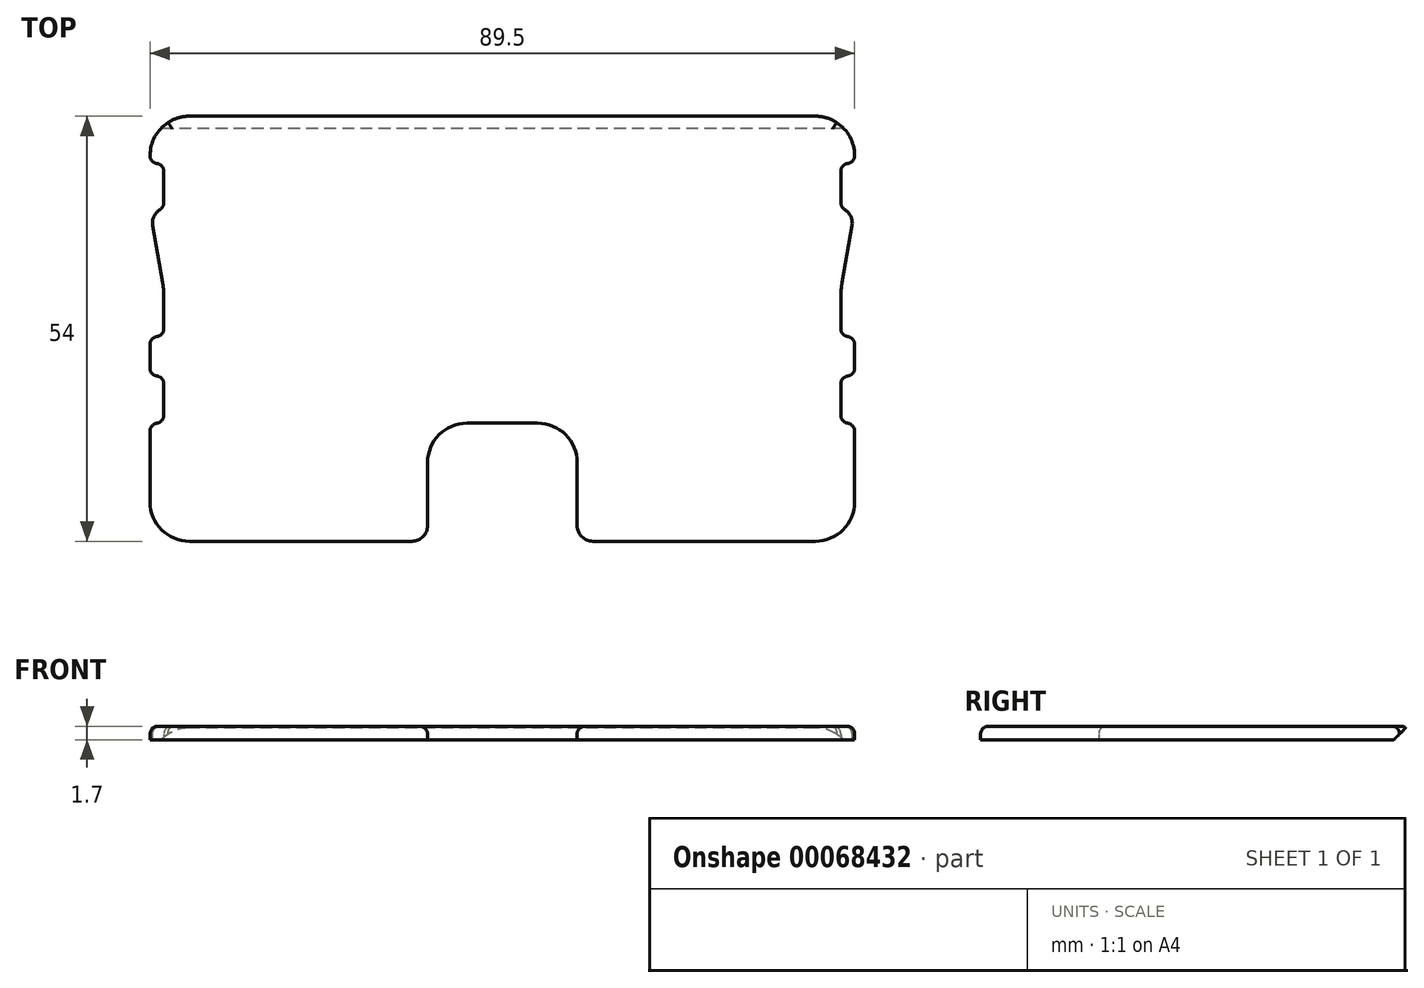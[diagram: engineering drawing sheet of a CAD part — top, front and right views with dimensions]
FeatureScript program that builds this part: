
annotation { "Feature Type Name" : "Feature", "Feature Type Description" : "" }
export const myFeature = defineFeature(function(context is Context, id is Id, definition is map)
    precondition{}
    {
        {
            var Q0;
            Q0=qCreatedBy(makeId("Top.planeOp"),FACE);
            var sketch = newSketch(context, id + "F0", { "sketchPlane" : qUnion([Q0])});
            skLineSegment(sketch, "E0", {"start": v(-44.75, -22.6) * mm, "end": v(-9.5, -22.6) * mm});
            skLineSegment(sketch, "E1", {"start": v(-9.5, -7.6) * mm, "end": v(9.5, -7.6) * mm});
            skLineSegment(sketch, "E2", {"start": v(9.5, -7.6) * mm, "end": v(9.5, -22.6) * mm});
            skLineSegment(sketch, "E3", {"start": v(9.5, -22.6) * mm, "end": v(44.75, -22.6) * mm});
            skLineSegment(sketch, "E4", {"start": v(44.75, -22.6) * mm, "end": v(44.75, -7.6) * mm});
            skLineSegment(sketch, "E5", {"start": v(44.75, -7.6) * mm, "end": v(43, -7.6) * mm});
            skLineSegment(sketch, "E6", {"start": v(43, -7.6) * mm, "end": v(43, -1.6) * mm});
            skLineSegment(sketch, "E7", {"start": v(43, -1.6) * mm, "end": v(44.75, -1.6) * mm});
            skLineSegment(sketch, "E8", {"start": v(44.75, -1.6) * mm, "end": v(44.75, 3.4) * mm});
            skLineSegment(sketch, "E9", {"start": v(44.75, 3.4) * mm, "end": v(43, 3.4) * mm});
            skLineSegment(sketch, "E10", {"start": v(43, 3.4) * mm, "end": v(43, 9.4) * mm});
            skLineSegment(sketch, "E11", {"start": v(43, 9.4) * mm, "end": v(44.75, 19.4) * mm});
            skPoint(sketch, "E11.endSnap0", {"position": v(44.75, 0.9) * mm});
            skLineSegment(sketch, "E12", {"start": v(44.75, 19.4) * mm, "end": v(43, 19.4) * mm});
            skPoint(sketch, "E12.endSnap0", {"position": v(43, 6.4) * mm});
            skLineSegment(sketch, "E13", {"start": v(43, 19.4) * mm, "end": v(43, 25.4) * mm});
            skLineSegment(sketch, "E14", {"start": v(43, 25.4) * mm, "end": v(44.75, 25.4) * mm});
            skLineSegment(sketch, "E15", {"start": v(44.75, 25.4) * mm, "end": v(44.75, 31.4) * mm});
            skLineSegment(sketch, "E16", {"start": v(44.75, 31.4) * mm, "end": v(-44.75, 31.4) * mm});
            skLineSegment(sketch, "E17", {"start": v(-44.75, 31.4) * mm, "end": v(-44.75, 25.4) * mm});
            skLineSegment(sketch, "E18", {"start": v(-44.75, 25.4) * mm, "end": v(-43, 25.4) * mm});
            skLineSegment(sketch, "E19", {"start": v(-43, 25.4) * mm, "end": v(-43, 19.4) * mm});
            skLineSegment(sketch, "E20", {"start": v(-43, 19.4) * mm, "end": v(-44.75, 19.4) * mm});
            skLineSegment(sketch, "E21", {"start": v(-44.75, 19.4) * mm, "end": v(-43, 9.4) * mm});
            skLineSegment(sketch, "E22", {"start": v(-43, 9.4) * mm, "end": v(-43, 3.4) * mm});
            skLineSegment(sketch, "E23", {"start": v(-43, 3.4) * mm, "end": v(-44.75, 3.4) * mm});
            skLineSegment(sketch, "E24", {"start": v(-44.75, 3.4) * mm, "end": v(-44.75, -1.6) * mm});
            skLineSegment(sketch, "E25", {"start": v(-44.75, -1.6) * mm, "end": v(-43, -1.6) * mm});
            skLineSegment(sketch, "E26", {"start": v(-43, -1.6) * mm, "end": v(-43, -7.6) * mm});
            skLineSegment(sketch, "E27", {"start": v(-43, -7.6) * mm, "end": v(-44.75, -7.6) * mm});
            skLineSegment(sketch, "E28", {"start": v(-44.75, -7.6) * mm, "end": v(-44.75, -22.6) * mm});
            skLineSegment(sketch, "E29", {"start": v(-9.5, -7.6) * mm, "end": v(-9.5, -22.6) * mm});
            skSolve(sketch);
        }
        {
            var Q0;
            Q0=makeQuery(id+"F0.imprint","IMPRINT",FACE,{"disambiguationData":[TD([[makeQuery(id+"F0.imprint","IMPRINT",EDGE,{"derivedFrom":sQuery(id+"F0.wireOp",EDGE,"E0")}),1.0]])]});
            extrude(context, id + "F1", {"entities" : qUnion([Q0]), "depth" : 1.7 * mm});
        }
        {
            var Q0;
            Q0=makeQuery(id+"F1.opExtrude","SWEPT_EDGE",EDGE,{"disambiguationData":[OSD([sQuery(id+"F0.wireOp",EDGE,"E18"),sQuery(id+"F0.wireOp",EDGE,"E19")])]});
            var Q1;
            Q1=makeQuery(id+"F1.opExtrude","SWEPT_EDGE",EDGE,{"disambiguationData":[OSD([sQuery(id+"F0.wireOp",EDGE,"E19"),sQuery(id+"F0.wireOp",EDGE,"E20")])]});
            var Q2;
            Q2=makeQuery(id+"F1.opExtrude","SWEPT_EDGE",EDGE,{"disambiguationData":[OSD([sQuery(id+"F0.wireOp",EDGE,"E22"),sQuery(id+"F0.wireOp",EDGE,"E23")])]});
            var Q3;
            Q3=makeQuery(id+"F1.opExtrude","SWEPT_EDGE",EDGE,{"disambiguationData":[OSD([sQuery(id+"F0.wireOp",EDGE,"E25"),sQuery(id+"F0.wireOp",EDGE,"E26")])]});
            var Q4;
            Q4=makeQuery(id+"F1.opExtrude","SWEPT_EDGE",EDGE,{"disambiguationData":[OSD([sQuery(id+"F0.wireOp",EDGE,"E26"),sQuery(id+"F0.wireOp",EDGE,"E27")])]});
            var Q5;
            Q5=makeQuery(id+"F1.opExtrude","SWEPT_EDGE",EDGE,{"disambiguationData":[OSD([sQuery(id+"F0.wireOp",EDGE,"E12"),sQuery(id+"F0.wireOp",EDGE,"E13")])]});
            var Q6;
            Q6=makeQuery(id+"F1.opExtrude","SWEPT_EDGE",EDGE,{"disambiguationData":[OSD([sQuery(id+"F0.wireOp",EDGE,"E13"),sQuery(id+"F0.wireOp",EDGE,"E14")])]});
            var Q7;
            Q7=makeQuery(id+"F1.opExtrude","SWEPT_EDGE",EDGE,{"disambiguationData":[OSD([sQuery(id+"F0.wireOp",EDGE,"E9"),sQuery(id+"F0.wireOp",EDGE,"E10")])]});
            var Q8;
            Q8=makeQuery(id+"F1.opExtrude","SWEPT_EDGE",EDGE,{"disambiguationData":[OSD([sQuery(id+"F0.wireOp",EDGE,"E5"),sQuery(id+"F0.wireOp",EDGE,"E6")])]});
            var Q9;
            Q9=makeQuery(id+"F1.opExtrude","SWEPT_EDGE",EDGE,{"disambiguationData":[OSD([sQuery(id+"F0.wireOp",EDGE,"E6"),sQuery(id+"F0.wireOp",EDGE,"E7")])]});
            fillet(context, id + "F2", {"entities" : qUnion([Q0, Q1, Q2, Q3, Q4, Q5, Q6, Q7, Q8, Q9]), "radius" : 1 * mm, "tangentPropagation" : true, "allowEdgeOverflow" : false});
        }
        {
            var Q0;
            Q0=makeQuery(id+"F1.opExtrude","SWEPT_EDGE",EDGE,{"disambiguationData":[OSD([sQuery(id+"F0.wireOp",EDGE,"E8"),sQuery(id+"F0.wireOp",EDGE,"E9")])]});
            var Q1;
            Q1=makeQuery(id+"F1.opExtrude","SWEPT_EDGE",EDGE,{"disambiguationData":[OSD([sQuery(id+"F0.wireOp",EDGE,"E4"),sQuery(id+"F0.wireOp",EDGE,"E5")])]});
            var Q2;
            Q2=makeQuery(id+"F1.opExtrude","SWEPT_EDGE",EDGE,{"disambiguationData":[OSD([sQuery(id+"F0.wireOp",EDGE,"E14"),sQuery(id+"F0.wireOp",EDGE,"E15")])]});
            var Q3;
            Q3=makeQuery(id+"F1.opExtrude","SWEPT_EDGE",EDGE,{"disambiguationData":[OSD([sQuery(id+"F0.wireOp",EDGE,"E7"),sQuery(id+"F0.wireOp",EDGE,"E8")])]});
            var Q4;
            Q4=makeQuery(id+"F1.opExtrude","SWEPT_EDGE",EDGE,{"disambiguationData":[OSD([sQuery(id+"F0.wireOp",EDGE,"E17"),sQuery(id+"F0.wireOp",EDGE,"E18")])]});
            var Q5;
            Q5=makeQuery(id+"F1.opExtrude","CAP_EDGE",EDGE,{"disambiguationData":[OSD([sQuery(id+"F0.wireOp",EDGE,"E26")])],"isStart":false});
            var Q6;
            Q6=makeQuery(id+"F1.opExtrude","CAP_EDGE",EDGE,{"disambiguationData":[OSD([sQuery(id+"F0.wireOp",EDGE,"E19")])],"isStart":false});
            var Q7;
            Q7=makeQuery(id+"F1.opExtrude","SWEPT_EDGE",EDGE,{"disambiguationData":[OSD([sQuery(id+"F0.wireOp",EDGE,"E24"),sQuery(id+"F0.wireOp",EDGE,"E25")])]});
            var Q8;
            Q8=makeQuery(id+"F1.opExtrude","SWEPT_EDGE",EDGE,{"disambiguationData":[OSD([sQuery(id+"F0.wireOp",EDGE,"E27"),sQuery(id+"F0.wireOp",EDGE,"E28")])]});
            var Q9;
            Q9=makeQuery(id+"F1.opExtrude","CAP_EDGE",EDGE,{"disambiguationData":[OSD([sQuery(id+"F0.wireOp",EDGE,"E13")])],"isStart":false});
            var Q10;
            Q10=makeQuery(id+"F1.opExtrude","CAP_EDGE",EDGE,{"disambiguationData":[OSD([sQuery(id+"F0.wireOp",EDGE,"E6")])],"isStart":false});
            var Q11;
            Q11=makeQuery(id+"F1.opExtrude","SWEPT_EDGE",EDGE,{"disambiguationData":[OSD([sQuery(id+"F0.wireOp",EDGE,"E23"),sQuery(id+"F0.wireOp",EDGE,"E24")])]});
            fillet(context, id + "F3", {"entities" : qUnion([Q0, Q1, Q2, Q3, Q4, Q5, Q6, Q7, Q8, Q9, Q10, Q11]), "radius" : 1 * mm, "tangentPropagation" : true, "allowEdgeOverflow" : false});
        }
        {
            var Q0;
            Q0=makeQuery(id+"F1.opExtrude","SWEPT_EDGE",EDGE,{"disambiguationData":[OSD([sQuery(id+"F0.wireOp",EDGE,"E21"),sQuery(id+"F0.wireOp",EDGE,"E22")])]});
            var Q1;
            Q1=makeQuery(id+"F1.opExtrude","SWEPT_EDGE",EDGE,{"disambiguationData":[OSD([sQuery(id+"F0.wireOp",EDGE,"E10"),sQuery(id+"F0.wireOp",EDGE,"E11")])]});
            fillet(context, id + "F4", {"entities" : qUnion([Q0, Q1]), "radius" : 10 * mm, "tangentPropagation" : true, "allowEdgeOverflow" : false});
        }
        {
            var Q0;
            Q0=makeQuery(id+"F1.opExtrude","SWEPT_EDGE",EDGE,{"disambiguationData":[OSD([sQuery(id+"F0.wireOp",EDGE,"E20"),sQuery(id+"F0.wireOp",EDGE,"E21")])]});
            var Q1;
            Q1=makeQuery(id+"F1.opExtrude","SWEPT_EDGE",EDGE,{"disambiguationData":[OSD([sQuery(id+"F0.wireOp",EDGE,"E11"),sQuery(id+"F0.wireOp",EDGE,"E12")])]});
            var Q2;
            Q2=makeQuery(id+"F1.opExtrude","SWEPT_EDGE",EDGE,{"disambiguationData":[OSD([sQuery(id+"F0.wireOp",EDGE,"E0"),sQuery(id+"F0.wireOp",EDGE,"E29")])]});
            var Q3;
            Q3=makeQuery(id+"F1.opExtrude","SWEPT_EDGE",EDGE,{"disambiguationData":[OSD([sQuery(id+"F0.wireOp",EDGE,"E2"),sQuery(id+"F0.wireOp",EDGE,"E3")])]});
            fillet(context, id + "F5", {"entities" : qUnion([Q0, Q1, Q2, Q3]), "radius" : 2 * mm, "allowEdgeOverflow" : false});
        }
        {
            var Q0;
            Q0=makeQuery(id+"F1.opExtrude","SWEPT_EDGE",EDGE,{"disambiguationData":[OSD([sQuery(id+"F0.wireOp",EDGE,"E1"),sQuery(id+"F0.wireOp",EDGE,"E2")])]});
            var Q1;
            Q1=makeQuery(id+"F1.opExtrude","SWEPT_EDGE",EDGE,{"disambiguationData":[OSD([sQuery(id+"F0.wireOp",EDGE,"E1"),sQuery(id+"F0.wireOp",EDGE,"E29")])]});
            fillet(context, id + "F6", {"entities" : qUnion([Q0, Q1]), "radius" : 5 * mm, "tangentPropagation" : true, "allowEdgeOverflow" : false});
        }
        {
            var Q0;
            Q0=makeQuery(id+"F1.opExtrude","CAP_EDGE",EDGE,{"disambiguationData":[OSD([sQuery(id+"F0.wireOp",EDGE,"E16")])],"isStart":true});
            chamfer(context, id + "F7", {"entities" : qUnion([Q0]), "width" : 1.5 * mm});
        }
        {
            var Q0;
            Q0=makeQuery(id+"F1.opExtrude","CAP_EDGE",EDGE,{"disambiguationData":[OSD([sQuery(id+"F0.wireOp",EDGE,"E10")])],"isStart":false});
            var Q1;
            Q1=makeQuery(id+"F1.opExtrude","CAP_EDGE",EDGE,{"disambiguationData":[OSD([sQuery(id+"F0.wireOp",EDGE,"E22")])],"isStart":false});
            fillet(context, id + "F8", {"entities" : qUnion([Q0, Q1]), "radius" : 1 * mm, "tangentPropagation" : true, "allowEdgeOverflow" : false});
        }
        {
            var Q0;
            Q0=makeQuery(id+"F1.opExtrude","SWEPT_EDGE",EDGE,{"disambiguationData":[OSD([sQuery(id+"F0.wireOp",EDGE,"E3"),sQuery(id+"F0.wireOp",EDGE,"E4")])]});
            var Q1;
            Q1=makeQuery(id+"F1.opExtrude","SWEPT_EDGE",EDGE,{"disambiguationData":[OSD([sQuery(id+"F0.wireOp",EDGE,"E15"),sQuery(id+"F0.wireOp",EDGE,"E16")])]});
            var Q2;
            Q2=makeQuery(id+"F1.opExtrude","SWEPT_EDGE",EDGE,{"disambiguationData":[OSD([sQuery(id+"F0.wireOp",EDGE,"E16"),sQuery(id+"F0.wireOp",EDGE,"E17")])]});
            var Q3;
            Q3=makeQuery(id+"F1.opExtrude","SWEPT_EDGE",EDGE,{"disambiguationData":[OSD([sQuery(id+"F0.wireOp",EDGE,"E0"),sQuery(id+"F0.wireOp",EDGE,"E28")])]});
            fillet(context, id + "F9", {"entities" : qUnion([Q0, Q1, Q2, Q3]), "radius" : 5 * mm, "tangentPropagation" : true, "allowEdgeOverflow" : false});
        }
        {
            var Q0;
            Q0=makeQuery(id+"F1.opExtrude","CAP_EDGE",EDGE,{"disambiguationData":[OSD([sQuery(id+"F0.wireOp",EDGE,"E28")])],"isStart":false});
            var Q1;
            {var subQ0=sQuery(id+"F0.wireOp",EDGE,"E17");var subQ1=sQuery(id+"F0.wireOp",EDGE,"E16");Q1=makeQuery(id+"F9.opFillet","BLEND_EDGE",EDGE,{"blendedFrom":[makeQuery(id+"F1.opExtrude","SWEPT_EDGE",EDGE,{"disambiguationData":[OSD([subQ1,subQ0])]}),makeQuery(id+"F1.opExtrude","CAP_FACE",FACE,{"disambiguationData":[OSD([sQuery(id+"F0.wireOp",EDGE,"E0"),sQuery(id+"F0.wireOp",EDGE,"E1"),sQuery(id+"F0.wireOp",EDGE,"E2"),sQuery(id+"F0.wireOp",EDGE,"E3"),sQuery(id+"F0.wireOp",EDGE,"E4"),sQuery(id+"F0.wireOp",EDGE,"E5"),sQuery(id+"F0.wireOp",EDGE,"E6"),sQuery(id+"F0.wireOp",EDGE,"E7"),sQuery(id+"F0.wireOp",EDGE,"E8"),sQuery(id+"F0.wireOp",EDGE,"E9"),sQuery(id+"F0.wireOp",EDGE,"E10"),sQuery(id+"F0.wireOp",EDGE,"E11"),sQuery(id+"F0.wireOp",EDGE,"E12"),sQuery(id+"F0.wireOp",EDGE,"E13"),sQuery(id+"F0.wireOp",EDGE,"E14"),sQuery(id+"F0.wireOp",EDGE,"E15"),subQ1,subQ0,sQuery(id+"F0.wireOp",EDGE,"E18"),sQuery(id+"F0.wireOp",EDGE,"E19"),sQuery(id+"F0.wireOp",EDGE,"E20"),sQuery(id+"F0.wireOp",EDGE,"E21"),sQuery(id+"F0.wireOp",EDGE,"E22"),sQuery(id+"F0.wireOp",EDGE,"E23"),sQuery(id+"F0.wireOp",EDGE,"E24"),sQuery(id+"F0.wireOp",EDGE,"E25"),sQuery(id+"F0.wireOp",EDGE,"E26"),sQuery(id+"F0.wireOp",EDGE,"E27"),sQuery(id+"F0.wireOp",EDGE,"E28"),sQuery(id+"F0.wireOp",EDGE,"E29")])],"isStart":false})],"blendedInto":[makeQuery(id+"F1.opExtrude","CAP_FACE",FACE,{"disambiguationData":[OSD([sQuery(id+"F0.wireOp",EDGE,"E0"),sQuery(id+"F0.wireOp",EDGE,"E1"),sQuery(id+"F0.wireOp",EDGE,"E2"),sQuery(id+"F0.wireOp",EDGE,"E3"),sQuery(id+"F0.wireOp",EDGE,"E4"),sQuery(id+"F0.wireOp",EDGE,"E5"),sQuery(id+"F0.wireOp",EDGE,"E6"),sQuery(id+"F0.wireOp",EDGE,"E7"),sQuery(id+"F0.wireOp",EDGE,"E8"),sQuery(id+"F0.wireOp",EDGE,"E9"),sQuery(id+"F0.wireOp",EDGE,"E10"),sQuery(id+"F0.wireOp",EDGE,"E11"),sQuery(id+"F0.wireOp",EDGE,"E12"),sQuery(id+"F0.wireOp",EDGE,"E13"),sQuery(id+"F0.wireOp",EDGE,"E14"),sQuery(id+"F0.wireOp",EDGE,"E15"),subQ1,subQ0,sQuery(id+"F0.wireOp",EDGE,"E18"),sQuery(id+"F0.wireOp",EDGE,"E19"),sQuery(id+"F0.wireOp",EDGE,"E20"),sQuery(id+"F0.wireOp",EDGE,"E21"),sQuery(id+"F0.wireOp",EDGE,"E22"),sQuery(id+"F0.wireOp",EDGE,"E23"),sQuery(id+"F0.wireOp",EDGE,"E24"),sQuery(id+"F0.wireOp",EDGE,"E25"),sQuery(id+"F0.wireOp",EDGE,"E26"),sQuery(id+"F0.wireOp",EDGE,"E27"),sQuery(id+"F0.wireOp",EDGE,"E28"),sQuery(id+"F0.wireOp",EDGE,"E29")])],"isStart":false})]});}
            fillet(context, id + "F10", {"entities" : qUnion([Q0, Q1]), "radius" : 1 * mm, "tangentPropagation" : true, "allowEdgeOverflow" : false});
        }
    });
